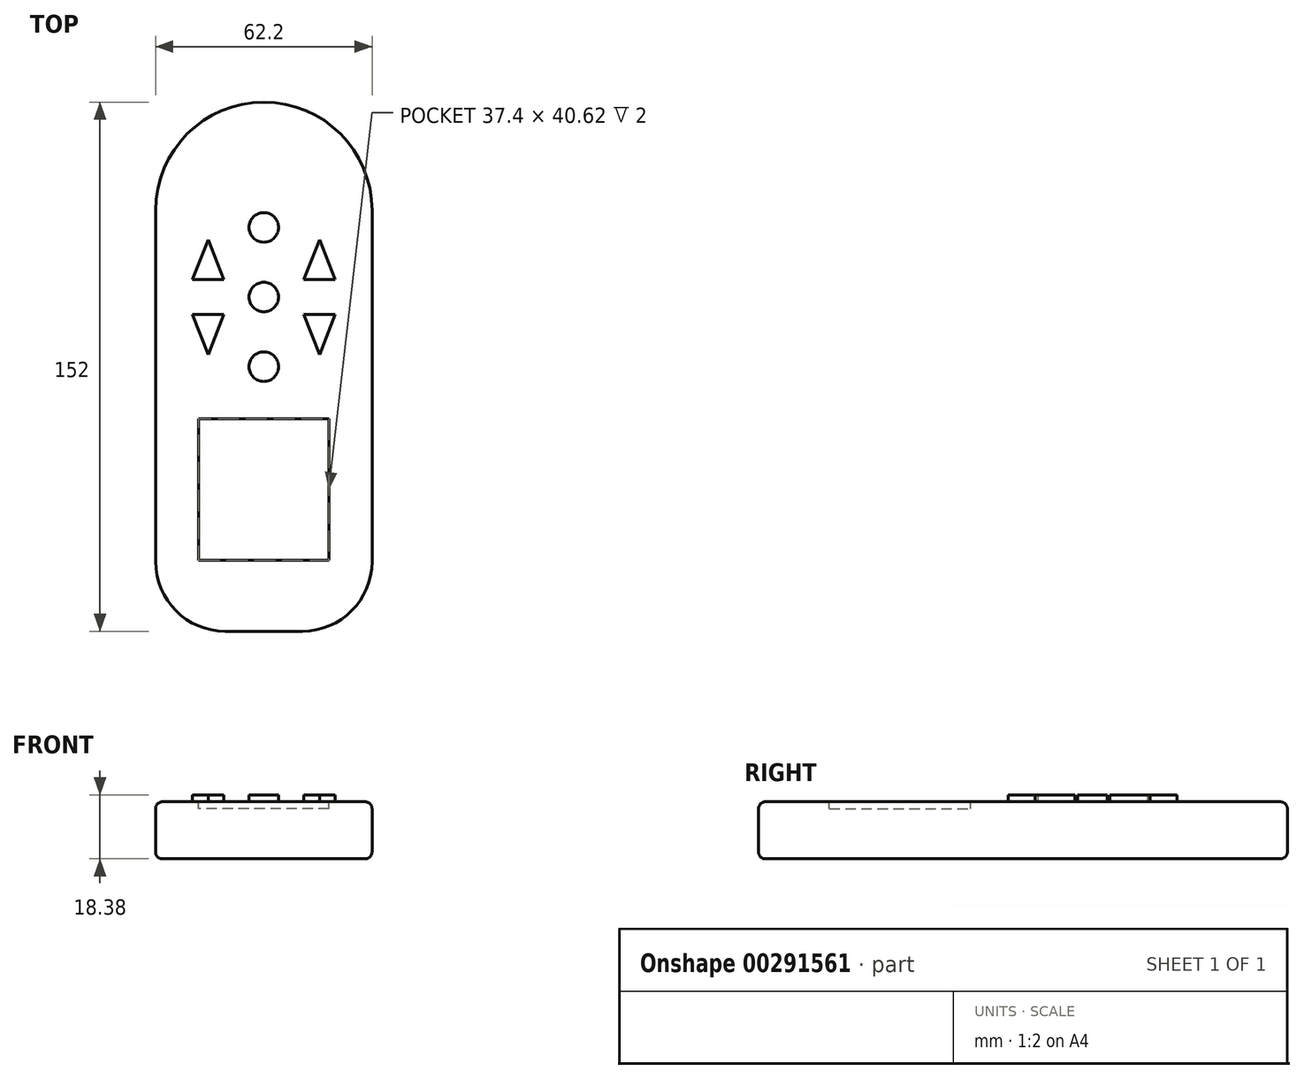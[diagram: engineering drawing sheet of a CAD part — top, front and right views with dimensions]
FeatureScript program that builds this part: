
annotation { "Feature Type Name" : "Feature", "Feature Type Description" : "" }
export const myFeature = defineFeature(function(context is Context, id is Id, definition is map)
    precondition{}
    {
        {
            var Q0;
            Q0=qCreatedBy(makeId("Top.planeOp"),FACE);
            var sketch = newSketch(context, id + "F0", { "sketchPlane" : qUnion([Q0])});
            skLineSegment(sketch, "E0.bottom", {"start": v(-31.1, 76) * mm, "end": v(31.1, 76) * mm});
            skLineSegment(sketch, "E0.top", {"start": v(-31.1, -76) * mm, "end": v(31.1, -76) * mm});
            skLineSegment(sketch, "E0.left", {"start": v(-31.1, 76) * mm, "end": v(-31.1, -76) * mm});
            skLineSegment(sketch, "E0.right", {"start": v(31.1, 76) * mm, "end": v(31.1, -76) * mm});
            skSolve(sketch);
        }
        {
            var Q0;
            Q0=makeQuery(id+"F0.imprint","IMPRINT",FACE,{"disambiguationData":[TD([[makeQuery(id+"F0.imprint","IMPRINT",EDGE,{"derivedFrom":sQuery(id+"F0.wireOp",EDGE,"E0.bottom")}),-1.0]])]});
            extrude(context, id + "F1", {"entities" : qUnion([Q0]), "depth" : 16.38 * mm});
        }
        {
            var Q0;
            Q0=makeQuery(id+"F1.opExtrude","SWEPT_EDGE",EDGE,{"disambiguationData":[OSD([sQuery(id+"F0.wireOp",EDGE,"E0.top"),sQuery(id+"F0.wireOp",EDGE,"E0.left")])]});
            var Q1;
            Q1=makeQuery(id+"F1.opExtrude","SWEPT_EDGE",EDGE,{"disambiguationData":[OSD([sQuery(id+"F0.wireOp",EDGE,"E0.top"),sQuery(id+"F0.wireOp",EDGE,"E0.right")])]});
            fillet(context, id + "F2", {"entities" : qUnion([Q0, Q1]), "radius" : 20 * mm, "tangentPropagation" : true, "allowEdgeOverflow" : false});
        }
        {
            var Q0;
            Q0=makeQuery(id+"F1.opExtrude","SWEPT_EDGE",EDGE,{"disambiguationData":[OSD([sQuery(id+"F0.wireOp",EDGE,"E0.bottom"),sQuery(id+"F0.wireOp",EDGE,"E0.right")])]});
            var Q1;
            Q1=makeQuery(id+"F1.opExtrude","SWEPT_EDGE",EDGE,{"disambiguationData":[OSD([sQuery(id+"F0.wireOp",EDGE,"E0.bottom"),sQuery(id+"F0.wireOp",EDGE,"E0.left")])]});
            fillet(context, id + "F3", {"entities" : qUnion([Q0, Q1]), "radius" : 31.1 * mm, "tangentPropagation" : true, "allowEdgeOverflow" : false});
        }
        {
            var Q0;
            Q0=makeQuery(id+"F1.opExtrude","CAP_EDGE",EDGE,{"disambiguationData":[OSD([sQuery(id+"F0.wireOp",EDGE,"E0.right")])],"isStart":false});
            var Q1;
            Q1=makeQuery(id+"F1.opExtrude","CAP_EDGE",EDGE,{"disambiguationData":[OSD([sQuery(id+"F0.wireOp",EDGE,"E0.right")])],"isStart":true});
            fillet(context, id + "F4", {"entities" : qUnion([Q0, Q1]), "radius" : 2 * mm, "tangentPropagation" : true, "allowEdgeOverflow" : false});
        }
        {
            var Q0;
            Q0=makeQuery(id+"F1.opExtrude","CAP_FACE",FACE,{"disambiguationData":[OSD([sQuery(id+"F0.wireOp",EDGE,"E0.bottom"),sQuery(id+"F0.wireOp",EDGE,"E0.top"),sQuery(id+"F0.wireOp",EDGE,"E0.left"),sQuery(id+"F0.wireOp",EDGE,"E0.right")])],"isStart":false});
            var sketch = newSketch(context, id + "F5", { "sketchPlane" : qUnion([Q0])});
            skLineSegment(sketch, "E1.bottom", {"start": v(18.7, -55.62) * mm, "end": v(-18.7, -55.62) * mm});
            skLineSegment(sketch, "E1.top", {"start": v(18.7, -15) * mm, "end": v(-18.7, -15) * mm});
            skLineSegment(sketch, "E1.left", {"start": v(18.7, -55.62) * mm, "end": v(18.7, -15) * mm});
            skLineSegment(sketch, "E1.right", {"start": v(-18.7, -55.62) * mm, "end": v(-18.7, -15) * mm});
            skSolve(sketch);
        }
        {
            var Q0;
            Q0=makeQuery(id+"F5.imprint","IMPRINT",FACE,{"disambiguationData":[TD([[makeQuery(id+"F5.imprint","IMPRINT",EDGE,{"derivedFrom":sQuery(id+"F5.wireOp",EDGE,"E1.bottom")}),-1.0]])]});
            extrude(context, id + "F6", {"entities" : qUnion([Q0]), "operationType" : NewBodyOperationType.REMOVE, "oppositeDirection" : true, "depth" : 2 * mm});
        }
        {
            var Q0;
            Q0=makeQuery(id+"F1.opExtrude","CAP_FACE",FACE,{"disambiguationData":[OSD([sQuery(id+"F0.wireOp",EDGE,"E0.bottom"),sQuery(id+"F0.wireOp",EDGE,"E0.top"),sQuery(id+"F0.wireOp",EDGE,"E0.left"),sQuery(id+"F0.wireOp",EDGE,"E0.right")])],"isStart":false});
            var sketch = newSketch(context, id + "F7", { "sketchPlane" : qUnion([Q0])});
            skCircle(sketch, "E2", {"center": v(0, 0) * mm, "radius": 4.25 * mm});
            skCircle(sketch, "E3", {"center": v(0, 20) * mm, "radius": 4.25 * mm});
            skCircle(sketch, "E4", {"center": v(0, 40) * mm, "radius": 4.25 * mm});
            skLineSegment(sketch, "E5", {"start": v(10.87, 20) * mm, "end": v(-10.8, 20) * mm, "construction": true});
            skLineSegment(sketch, "E6", {"start": v(0, -7.57) * mm, "end": v(0, 40.8) * mm, "construction": true});
            skLineSegment(sketch, "E7", {"start": v(16, 3.5) * mm, "end": v(20.5, 15) * mm});
            skLineSegment(sketch, "E8", {"start": v(20.5, 15) * mm, "end": v(11.5, 15) * mm});
            skLineSegment(sketch, "E9", {"start": v(11.5, 15) * mm, "end": v(16, 3.5) * mm});
            skLineSegment(sketch, "E10.MirrorCS", {"start": v(20.5, 25) * mm, "end": v(11.5, 25) * mm});
            skLineSegment(sketch, "E11.MirrorCS", {"start": v(11.5, 25) * mm, "end": v(16, 36.5) * mm});
            skLineSegment(sketch, "E12.MirrorCS", {"start": v(16, 36.5) * mm, "end": v(20.5, 25) * mm});
            skLineSegment(sketch, "E13.MirrorCS", {"start": v(-11.5, 25) * mm, "end": v(-16, 36.5) * mm});
            skLineSegment(sketch, "E14.MirrorCS", {"start": v(-11.5, 15) * mm, "end": v(-16, 3.5) * mm});
            skLineSegment(sketch, "E15.MirrorCS", {"start": v(-20.5, 15) * mm, "end": v(-11.5, 15) * mm});
            skLineSegment(sketch, "E16.MirrorCS", {"start": v(-16, 3.5) * mm, "end": v(-20.5, 15) * mm});
            skLineSegment(sketch, "E17.MirrorCS", {"start": v(-16, 36.5) * mm, "end": v(-20.5, 25) * mm});
            skLineSegment(sketch, "E18.MirrorCS", {"start": v(-20.5, 25) * mm, "end": v(-11.5, 25) * mm});
            skSolve(sketch);
        }
        {
            var Q0;
            Q0=makeQuery(id+"F7.imprint","IMPRINT",FACE,{"disambiguationData":[TD([[makeQuery(id+"F7.imprint","IMPRINT",EDGE,{"derivedFrom":sQuery(id+"F7.wireOp",EDGE,"E7")}),1.0]])]});
            var Q1;
            Q1=makeQuery(id+"F7.imprint","IMPRINT",FACE,{"disambiguationData":[TD([[makeQuery(id+"F7.imprint","IMPRINT",EDGE,{"derivedFrom":sQuery(id+"F7.wireOp",EDGE,"E2")}),1.0]])]});
            var Q2;
            Q2=makeQuery(id+"F7.imprint","IMPRINT",FACE,{"disambiguationData":[TD([[makeQuery(id+"F7.imprint","IMPRINT",EDGE,{"derivedFrom":sQuery(id+"F7.wireOp",EDGE,"E14.MirrorCS")}),-1.0]])]});
            var Q3;
            Q3=makeQuery(id+"F7.imprint","IMPRINT",FACE,{"disambiguationData":[TD([[makeQuery(id+"F7.imprint","IMPRINT",EDGE,{"derivedFrom":sQuery(id+"F7.wireOp",EDGE,"E13.MirrorCS")}),1.0]])]});
            var Q4;
            Q4=makeQuery(id+"F7.imprint","IMPRINT",FACE,{"disambiguationData":[TD([[makeQuery(id+"F7.imprint","IMPRINT",EDGE,{"derivedFrom":sQuery(id+"F7.wireOp",EDGE,"E3")}),1.0]])]});
            var Q5;
            Q5=makeQuery(id+"F7.imprint","IMPRINT",FACE,{"disambiguationData":[TD([[makeQuery(id+"F7.imprint","IMPRINT",EDGE,{"derivedFrom":sQuery(id+"F7.wireOp",EDGE,"E10.MirrorCS")}),-1.0]])]});
            var Q6;
            Q6=makeQuery(id+"F7.imprint","IMPRINT",FACE,{"disambiguationData":[TD([[makeQuery(id+"F7.imprint","IMPRINT",EDGE,{"derivedFrom":sQuery(id+"F7.wireOp",EDGE,"E4")}),1.0]])]});
            extrude(context, id + "F8", {"entities" : qUnion([Q0, Q1, Q2, Q3, Q4, Q5, Q6]), "operationType" : NewBodyOperationType.ADD, "depth" : 2 * mm});
        }
    });
